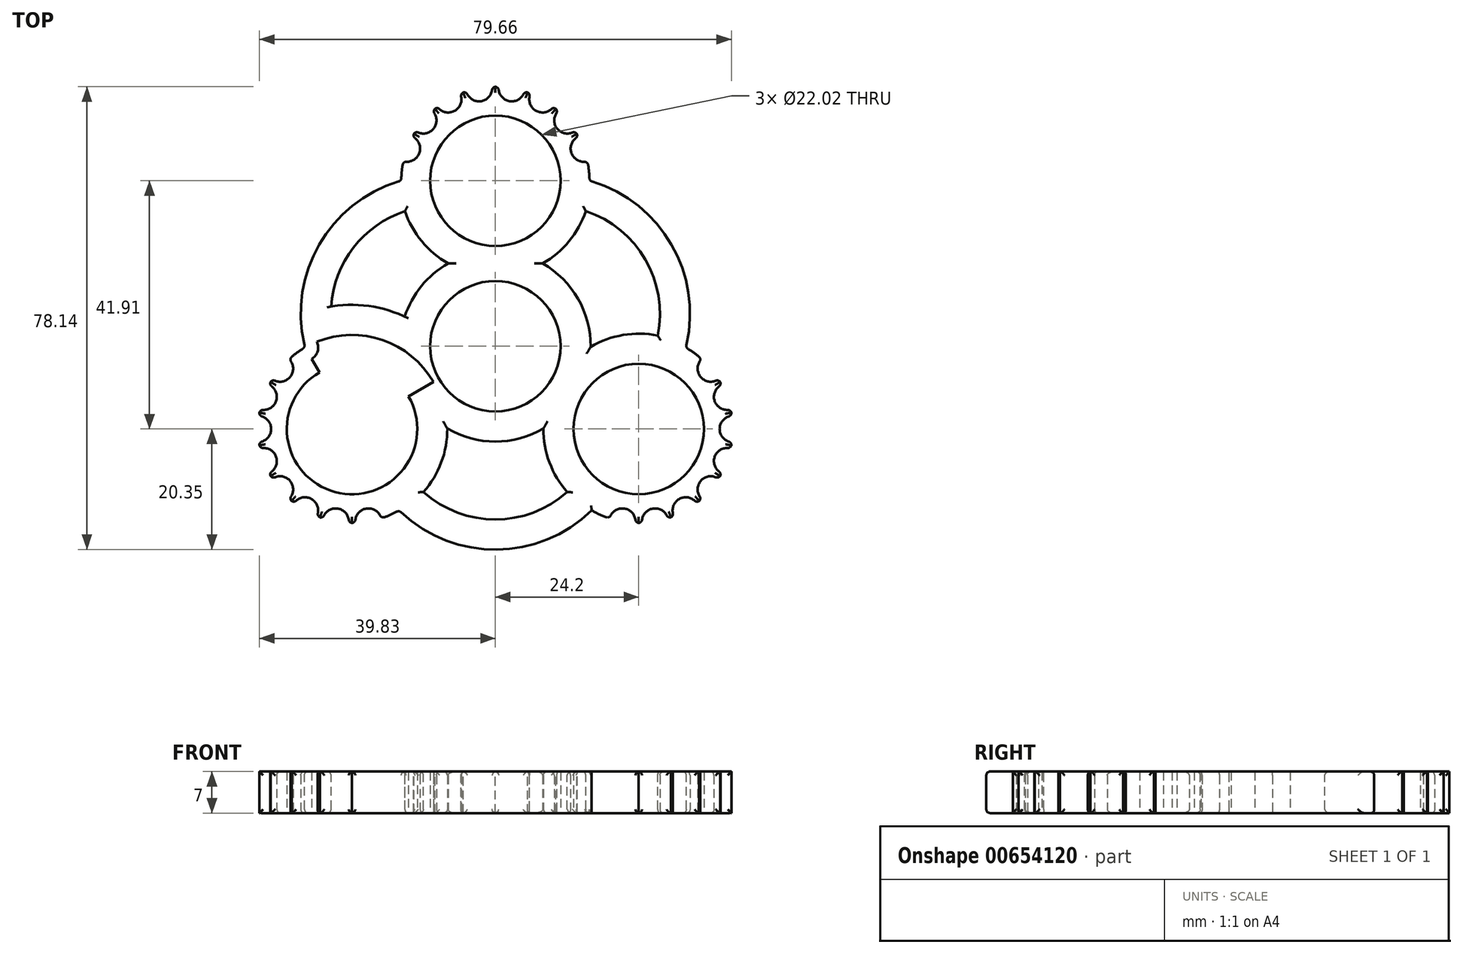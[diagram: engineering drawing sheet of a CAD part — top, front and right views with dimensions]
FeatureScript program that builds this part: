
annotation { "Feature Type Name" : "Feature", "Feature Type Description" : "" }
export const myFeature = defineFeature(function(context is Context, id is Id, definition is map)
    precondition{}
    {
        {
            var Q0;
            Q0=qCreatedBy(makeId("Top.planeOp"),FACE);
            var sketch = newSketch(context, id + "F0", { "sketchPlane" : qUnion([Q0])});
            skCircle(sketch, "E0", {"center": v(0, 0) * mm, "radius": 11.01 * mm});
            skCircle(sketch, "E1", {"center": v(0, 27.94) * mm, "radius": 11.01 * mm});
            skCircle(sketch, "E2", {"center": v(24.2, -13.97) * mm, "radius": 11.01 * mm});
            skCircle(sketch, "E3", {"center": v(-24.2, -13.97) * mm, "radius": 11.01 * mm});
            skLineSegment(sketch, "E4", {"start": v(-24.2, -13.97) * mm, "end": v(0, 0) * mm});
            skLineSegment(sketch, "E5", {"start": v(0, 0) * mm, "end": v(24.2, -13.97) * mm});
            skLineSegment(sketch, "E6", {"start": v(0, 0) * mm, "end": v(0, 27.94) * mm});
            skCircle(sketch, "E7", {"center": v(0, 27.94) * mm, "radius": 15.88 * mm});
            skCircle(sketch, "E8", {"center": v(24.2, -13.97) * mm, "radius": 15.88 * mm});
            skCircle(sketch, "E9", {"center": v(-24.2, -13.97) * mm, "radius": 15.88 * mm});
            skArc(sketch, "E10", {"start": v(-15.88, 27.94) * mm, "mid": v(-29.73, 17.16) * mm, "end": v(-32.13, -0.22) * mm});
            skArc(sketch, "E11", {"start": v(32.13, -0.22) * mm, "mid": v(29.73, 17.16) * mm, "end": v(15.88, 27.94) * mm});
            skArc(sketch, "E12", {"start": v(-16.26, -27.72) * mm, "mid": v(0, -34.32) * mm, "end": v(16.26, -27.72) * mm});
            skLineSegment(sketch, "E13", {"start": v(-15.88, 27.94) * mm, "end": v(15.88, 27.94) * mm});
            skLineSegment(sketch, "E14", {"start": v(-16.26, -27.72) * mm, "end": v(-32.13, -0.22) * mm});
            skLineSegment(sketch, "E15", {"start": v(32.13, -0.22) * mm, "end": v(16.26, -27.72) * mm});
            skLineSegment(sketch, "E16", {"start": v(-24.2, -13.97) * mm, "end": v(-37.94, -21.9) * mm});
            skLineSegment(sketch, "E17", {"start": v(0, 27.94) * mm, "end": v(0, 43.82) * mm});
            skLineSegment(sketch, "E18", {"start": v(24.2, -13.97) * mm, "end": v(37.94, -21.9) * mm});
            skCircle(sketch, "E19", {"center": v(-16.26, -27.72) * mm, "radius": 2.22 * mm});
            skCircle(sketch, "E20.1.0", {"center": v(-21.44, -29.6) * mm, "radius": 2.22 * mm});
            skCircle(sketch, "E20.2.0", {"center": v(-26.95, -29.6) * mm, "radius": 2.22 * mm});
            skCircle(sketch, "E20.3.0", {"center": v(-32.13, -27.72) * mm, "radius": 2.22 * mm});
            skCircle(sketch, "E20.4.0", {"center": v(-36.36, -24.17) * mm, "radius": 2.22 * mm});
            skCircle(sketch, "E20.5.0", {"center": v(-39.11, -19.4) * mm, "radius": 2.22 * mm});
            skCircle(sketch, "E20.6.0", {"center": v(-40.07, -13.97) * mm, "radius": 2.22 * mm});
            skCircle(sketch, "E20.7.0", {"center": v(-39.11, -8.54) * mm, "radius": 2.22 * mm});
            skCircle(sketch, "E20.8.0", {"center": v(-36.36, -3.77) * mm, "radius": 2.22 * mm});
            skCircle(sketch, "E20.9.0", {"center": v(-32.13, -0.22) * mm, "radius": 2.22 * mm});
            skLineSegment(sketch, "E20.anchor1", {"start": v(-24.2, -13.97) * mm, "end": v(-16.26, -27.72) * mm, "construction": true});
            skLineSegment(sketch, "E20.anchor2", {"start": v(-24.2, -13.97) * mm, "end": v(-32.13, -0.22) * mm, "construction": true});
            skCircle(sketch, "E21", {"center": v(-15.88, 27.94) * mm, "radius": 2.22 * mm});
            skCircle(sketch, "E22", {"center": v(32.13, -0.22) * mm, "radius": 2.22 * mm});
            skCircle(sketch, "E23.1.0", {"center": v(-14.92, 33.37) * mm, "radius": 2.22 * mm});
            skCircle(sketch, "E23.2.0", {"center": v(-12.16, 38.14) * mm, "radius": 2.22 * mm});
            skCircle(sketch, "E23.3.0", {"center": v(-7.94, 41.69) * mm, "radius": 2.22 * mm});
            skCircle(sketch, "E23.4.0", {"center": v(-2.76, 43.57) * mm, "radius": 2.22 * mm});
            skCircle(sketch, "E23.5.0", {"center": v(2.76, 43.57) * mm, "radius": 2.22 * mm});
            skCircle(sketch, "E23.6.0", {"center": v(7.94, 41.69) * mm, "radius": 2.22 * mm});
            skCircle(sketch, "E23.7.0", {"center": v(12.16, 38.14) * mm, "radius": 2.22 * mm});
            skCircle(sketch, "E23.8.0", {"center": v(14.92, 33.37) * mm, "radius": 2.22 * mm});
            skCircle(sketch, "E23.9.0", {"center": v(15.88, 27.94) * mm, "radius": 2.22 * mm});
            skLineSegment(sketch, "E23.anchor1", {"start": v(0, 27.94) * mm, "end": v(-15.88, 27.94) * mm, "construction": true});
            skLineSegment(sketch, "E23.anchor2", {"start": v(0, 27.94) * mm, "end": v(15.88, 27.94) * mm, "construction": true});
            skCircle(sketch, "E24.1.0", {"center": v(36.36, -3.77) * mm, "radius": 2.22 * mm});
            skCircle(sketch, "E24.2.0", {"center": v(39.11, -8.54) * mm, "radius": 2.22 * mm});
            skCircle(sketch, "E24.3.0", {"center": v(40.07, -13.97) * mm, "radius": 2.22 * mm});
            skCircle(sketch, "E24.4.0", {"center": v(39.11, -19.4) * mm, "radius": 2.22 * mm});
            skCircle(sketch, "E24.5.0", {"center": v(36.36, -24.17) * mm, "radius": 2.22 * mm});
            skCircle(sketch, "E24.6.0", {"center": v(32.13, -27.72) * mm, "radius": 2.22 * mm});
            skCircle(sketch, "E24.7.0", {"center": v(26.95, -29.6) * mm, "radius": 2.22 * mm});
            skCircle(sketch, "E24.8.0", {"center": v(21.44, -29.6) * mm, "radius": 2.22 * mm});
            skCircle(sketch, "E24.9.0", {"center": v(16.26, -27.72) * mm, "radius": 2.22 * mm});
            skLineSegment(sketch, "E24.anchor1", {"start": v(24.2, -13.97) * mm, "end": v(32.13, -0.22) * mm, "construction": true});
            skLineSegment(sketch, "E24.anchor2", {"start": v(24.2, -13.97) * mm, "end": v(16.26, -27.72) * mm, "construction": true});
            skSolve(sketch);
        }
        {
            var Q0;
            {var subQ1=sQuery(id+"F0.wireOp",EDGE,"E7");var subQ3=sQuery(id+"F0.wireOp",EDGE,"E23.9.0");var subQ4=makeQuery(id+"F0.imprint","INTERSECT",VERTEX,{"disambiguationData":[OD(0.0)],"derivedFrom":[subQ1,subQ3]});Q0=makeQuery(id+"F0.imprint","IMPRINT",FACE,{"disambiguationData":[TD([[makeQuery(id+"F0.imprint","IMPRINT",EDGE,{"disambiguationData":[TD([[subQ4,-1.0]])],"derivedFrom":subQ3}),1.0]])]});}
            var Q1;
            {var subQ1=sQuery(id+"F0.wireOp",EDGE,"E7");var subQ3=sQuery(id+"F0.wireOp",EDGE,"E21");var subQ4=makeQuery(id+"F0.imprint","INTERSECT",VERTEX,{"disambiguationData":[OD(0.0)],"derivedFrom":[subQ1,subQ3]});Q1=makeQuery(id+"F0.imprint","IMPRINT",FACE,{"disambiguationData":[TD([[makeQuery(id+"F0.imprint","IMPRINT",EDGE,{"disambiguationData":[TD([[subQ4,1.0]])],"derivedFrom":subQ3}),1.0]])]});}
            var Q2;
            {var subQ0=sQuery(id+"F0.wireOp",EDGE,"E10");var subQ3=sQuery(id+"F0.wireOp",EDGE,"E21");var subQ5=makeQuery(id+"F0.imprint","INTERSECT",VERTEX,{"derivedFrom":[subQ0,subQ3]});Q2=makeQuery(id+"F0.imprint","IMPRINT",FACE,{"disambiguationData":[TD([[makeQuery(id+"F0.imprint","IMPRINT",EDGE,{"disambiguationData":[TD([[subQ5,-1.0]])],"derivedFrom":subQ3}),1.0]])]});}
            var Q3;
            {var subQ0=sQuery(id+"F0.wireOp",EDGE,"E11");var subQ3=sQuery(id+"F0.wireOp",EDGE,"E23.9.0");var subQ5=makeQuery(id+"F0.imprint","INTERSECT",VERTEX,{"derivedFrom":[subQ0,subQ3]});Q3=makeQuery(id+"F0.imprint","IMPRINT",FACE,{"disambiguationData":[TD([[makeQuery(id+"F0.imprint","IMPRINT",EDGE,{"disambiguationData":[TD([[subQ5,1.0]])],"derivedFrom":subQ3}),1.0]])]});}
            var Q4;
            {var subQ1=sQuery(id+"F0.wireOp",EDGE,"E8");var subQ3=sQuery(id+"F0.wireOp",EDGE,"E22");var subQ4=makeQuery(id+"F0.imprint","INTERSECT",VERTEX,{"disambiguationData":[OD(0.0)],"derivedFrom":[subQ1,subQ3]});Q4=makeQuery(id+"F0.imprint","IMPRINT",FACE,{"disambiguationData":[TD([[makeQuery(id+"F0.imprint","IMPRINT",EDGE,{"disambiguationData":[TD([[subQ4,1.0]])],"derivedFrom":subQ3}),1.0]])]});}
            var Q5;
            {var subQ0=sQuery(id+"F0.wireOp",EDGE,"E11");var subQ3=sQuery(id+"F0.wireOp",EDGE,"E22");var subQ5=makeQuery(id+"F0.imprint","INTERSECT",VERTEX,{"derivedFrom":[subQ0,subQ3]});Q5=makeQuery(id+"F0.imprint","IMPRINT",FACE,{"disambiguationData":[TD([[makeQuery(id+"F0.imprint","IMPRINT",EDGE,{"disambiguationData":[TD([[subQ5,-1.0]])],"derivedFrom":subQ3}),1.0]])]});}
            var Q6;
            {var subQ0=sQuery(id+"F0.wireOp",EDGE,"E12");var subQ3=sQuery(id+"F0.wireOp",EDGE,"E24.9.0");var subQ5=makeQuery(id+"F0.imprint","INTERSECT",VERTEX,{"derivedFrom":[subQ0,subQ3]});Q6=makeQuery(id+"F0.imprint","IMPRINT",FACE,{"disambiguationData":[TD([[makeQuery(id+"F0.imprint","IMPRINT",EDGE,{"disambiguationData":[TD([[subQ5,1.0]])],"derivedFrom":subQ3}),1.0]])]});}
            var Q7;
            {var subQ1=sQuery(id+"F0.wireOp",EDGE,"E8");var subQ3=sQuery(id+"F0.wireOp",EDGE,"E24.9.0");var subQ4=makeQuery(id+"F0.imprint","INTERSECT",VERTEX,{"disambiguationData":[OD(0.0)],"derivedFrom":[subQ1,subQ3]});Q7=makeQuery(id+"F0.imprint","IMPRINT",FACE,{"disambiguationData":[TD([[makeQuery(id+"F0.imprint","IMPRINT",EDGE,{"disambiguationData":[TD([[subQ4,-1.0]])],"derivedFrom":subQ3}),1.0]])]});}
            var Q8;
            {var subQ0=sQuery(id+"F0.wireOp",EDGE,"E10");var subQ3=sQuery(id+"F0.wireOp",EDGE,"E20.9.0");var subQ5=makeQuery(id+"F0.imprint","INTERSECT",VERTEX,{"derivedFrom":[subQ0,subQ3]});Q8=makeQuery(id+"F0.imprint","IMPRINT",FACE,{"disambiguationData":[TD([[makeQuery(id+"F0.imprint","IMPRINT",EDGE,{"disambiguationData":[TD([[subQ5,1.0]])],"derivedFrom":subQ3}),1.0]])]});}
            var Q9;
            {var subQ1=sQuery(id+"F0.wireOp",EDGE,"E9");var subQ3=sQuery(id+"F0.wireOp",EDGE,"E20.9.0");var subQ4=makeQuery(id+"F0.imprint","INTERSECT",VERTEX,{"disambiguationData":[OD(0.0)],"derivedFrom":[subQ1,subQ3]});Q9=makeQuery(id+"F0.imprint","IMPRINT",FACE,{"disambiguationData":[TD([[makeQuery(id+"F0.imprint","IMPRINT",EDGE,{"disambiguationData":[TD([[subQ4,-1.0]])],"derivedFrom":subQ3}),1.0]])]});}
            var Q10;
            {var subQ1=sQuery(id+"F0.wireOp",EDGE,"E9");var subQ3=sQuery(id+"F0.wireOp",EDGE,"E19");var subQ4=makeQuery(id+"F0.imprint","INTERSECT",VERTEX,{"disambiguationData":[OD(0.0)],"derivedFrom":[subQ1,subQ3]});Q10=makeQuery(id+"F0.imprint","IMPRINT",FACE,{"disambiguationData":[TD([[makeQuery(id+"F0.imprint","IMPRINT",EDGE,{"disambiguationData":[TD([[subQ4,1.0]])],"derivedFrom":subQ3}),1.0]])]});}
            var Q11;
            {var subQ0=sQuery(id+"F0.wireOp",EDGE,"E12");var subQ3=sQuery(id+"F0.wireOp",EDGE,"E19");var subQ5=makeQuery(id+"F0.imprint","INTERSECT",VERTEX,{"derivedFrom":[subQ0,subQ3]});Q11=makeQuery(id+"F0.imprint","IMPRINT",FACE,{"disambiguationData":[TD([[makeQuery(id+"F0.imprint","IMPRINT",EDGE,{"disambiguationData":[TD([[subQ5,-1.0]])],"derivedFrom":subQ3}),1.0]])]});}
            var Q12;
            {var subQ7=sQuery(id+"F0.wireOp",EDGE,"E0");var subQ9=sQuery(id+"F0.wireOp",EDGE,"E4");var subQ10=makeQuery(id+"F0.imprint","INTERSECT",VERTEX,{"derivedFrom":[subQ7,subQ9]});Q12=makeQuery(id+"F0.imprint","IMPRINT",FACE,{"disambiguationData":[TD([[makeQuery(id+"F0.imprint","IMPRINT",EDGE,{"disambiguationData":[TD([[subQ10,1.0]])],"derivedFrom":subQ7}),-1.0]])]});}
            var Q13;
            {var subQ5=sQuery(id+"F0.wireOp",EDGE,"E0");var subQ7=sQuery(id+"F0.wireOp",EDGE,"E4");var subQ8=makeQuery(id+"F0.imprint","INTERSECT",VERTEX,{"derivedFrom":[subQ5,subQ7]});Q13=makeQuery(id+"F0.imprint","IMPRINT",FACE,{"disambiguationData":[TD([[makeQuery(id+"F0.imprint","IMPRINT",EDGE,{"disambiguationData":[TD([[subQ8,-1.0]])],"derivedFrom":subQ5}),-1.0]])]});}
            var Q14;
            {var subQ1=sQuery(id+"F0.wireOp",EDGE,"E6");var subQ7=sQuery(id+"F0.wireOp",EDGE,"E0");var subQ8=makeQuery(id+"F0.imprint","INTERSECT",VERTEX,{"derivedFrom":[subQ7,subQ1]});Q14=makeQuery(id+"F0.imprint","IMPRINT",FACE,{"disambiguationData":[TD([[makeQuery(id+"F0.imprint","IMPRINT",EDGE,{"disambiguationData":[TD([[subQ8,1.0]])],"derivedFrom":subQ7}),-1.0]])]});}
            var Q15;
            {var subQ1=sQuery(id+"F0.wireOp",EDGE,"E1");var subQ10=sQuery(id+"F0.wireOp",EDGE,"E17");var subQ13=makeQuery(id+"F0.imprint","INTERSECT",VERTEX,{"derivedFrom":[subQ1,subQ10]});Q15=makeQuery(id+"F0.imprint","IMPRINT",FACE,{"disambiguationData":[TD([[makeQuery(id+"F0.imprint","IMPRINT",EDGE,{"disambiguationData":[TD([[subQ13,1.0]])],"derivedFrom":subQ1}),-1.0]])]});}
            var Q16;
            {var subQ4=sQuery(id+"F0.wireOp",EDGE,"E17");var subQ5=sQuery(id+"F0.wireOp",EDGE,"E1");var subQ6=makeQuery(id+"F0.imprint","INTERSECT",VERTEX,{"derivedFrom":[subQ5,subQ4]});Q16=makeQuery(id+"F0.imprint","IMPRINT",FACE,{"disambiguationData":[TD([[makeQuery(id+"F0.imprint","IMPRINT",EDGE,{"disambiguationData":[TD([[subQ6,-1.0]])],"derivedFrom":subQ5}),-1.0]])]});}
            var Q17;
            {var subQ6=sQuery(id+"F0.wireOp",EDGE,"E2");var subQ12=sQuery(id+"F0.wireOp",EDGE,"E15");var subQ13=makeQuery(id+"F0.imprint","INTERSECT",VERTEX,{"disambiguationData":[OD(1.0)],"derivedFrom":[subQ6,subQ12]});Q17=makeQuery(id+"F0.imprint","IMPRINT",FACE,{"disambiguationData":[TD([[makeQuery(id+"F0.imprint","IMPRINT",EDGE,{"disambiguationData":[TD([[subQ13,-1.0]])],"derivedFrom":subQ6}),-1.0]])]});}
            var Q18;
            {var subQ6=sQuery(id+"F0.wireOp",EDGE,"E15");var subQ15=sQuery(id+"F0.wireOp",EDGE,"E2");var subQ17=makeQuery(id+"F0.imprint","INTERSECT",VERTEX,{"disambiguationData":[OD(0.0)],"derivedFrom":[subQ15,subQ6]});Q18=makeQuery(id+"F0.imprint","IMPRINT",FACE,{"disambiguationData":[TD([[makeQuery(id+"F0.imprint","IMPRINT",EDGE,{"disambiguationData":[TD([[subQ17,1.0]])],"derivedFrom":subQ15}),-1.0]])]});}
            var Q19;
            {var subQ3=sQuery(id+"F0.wireOp",EDGE,"E3");var subQ5=sQuery(id+"F0.wireOp",EDGE,"E14");var subQ6=makeQuery(id+"F0.imprint","INTERSECT",VERTEX,{"disambiguationData":[OD(0.0)],"derivedFrom":[subQ3,subQ5]});Q19=makeQuery(id+"F0.imprint","IMPRINT",FACE,{"disambiguationData":[TD([[makeQuery(id+"F0.imprint","IMPRINT",EDGE,{"disambiguationData":[TD([[subQ6,-1.0]])],"derivedFrom":subQ3}),-1.0]])]});}
            var Q20;
            {var subQ4=sQuery(id+"F0.wireOp",EDGE,"E16");var subQ6=sQuery(id+"F0.wireOp",EDGE,"E3");var subQ7=makeQuery(id+"F0.imprint","INTERSECT",VERTEX,{"derivedFrom":[subQ6,subQ4]});Q20=makeQuery(id+"F0.imprint","IMPRINT",FACE,{"disambiguationData":[TD([[makeQuery(id+"F0.imprint","IMPRINT",EDGE,{"disambiguationData":[TD([[subQ7,-1.0]])],"derivedFrom":subQ6}),-1.0]])]});}
            var Q21;
            {var subQ0=sQuery(id+"F0.wireOp",EDGE,"E13");var subQ1=sQuery(id+"F0.wireOp",EDGE,"E1");var subQ2=makeQuery(id+"F0.imprint","INTERSECT",VERTEX,{"disambiguationData":[OD(1.0)],"derivedFrom":[subQ1,subQ0]});Q21=makeQuery(id+"F0.imprint","IMPRINT",FACE,{"disambiguationData":[TD([[makeQuery(id+"F0.imprint","IMPRINT",EDGE,{"disambiguationData":[TD([[subQ2,-1.0]])],"derivedFrom":subQ1}),-1.0]])]});}
            var Q22;
            {var subQ1=sQuery(id+"F0.wireOp",EDGE,"E7");var subQ3=sQuery(id+"F0.wireOp",EDGE,"E21");var subQ4=makeQuery(id+"F0.imprint","INTERSECT",VERTEX,{"disambiguationData":[OD(1.0)],"derivedFrom":[subQ1,subQ3]});Q22=makeQuery(id+"F0.imprint","IMPRINT",FACE,{"disambiguationData":[TD([[makeQuery(id+"F0.imprint","IMPRINT",EDGE,{"disambiguationData":[TD([[subQ4,-1.0]])],"derivedFrom":subQ3}),1.0]])]});}
            var Q23;
            {var subQ1=sQuery(id+"F0.wireOp",EDGE,"E7");var subQ3=sQuery(id+"F0.wireOp",EDGE,"E23.9.0");var subQ4=makeQuery(id+"F0.imprint","INTERSECT",VERTEX,{"disambiguationData":[OD(1.0)],"derivedFrom":[subQ1,subQ3]});Q23=makeQuery(id+"F0.imprint","IMPRINT",FACE,{"disambiguationData":[TD([[makeQuery(id+"F0.imprint","IMPRINT",EDGE,{"disambiguationData":[TD([[subQ4,1.0]])],"derivedFrom":subQ3}),1.0]])]});}
            var Q24;
            {var subQ0=sQuery(id+"F0.wireOp",EDGE,"E13");var subQ1=sQuery(id+"F0.wireOp",EDGE,"E1");var subQ2=makeQuery(id+"F0.imprint","INTERSECT",VERTEX,{"disambiguationData":[OD(0.0)],"derivedFrom":[subQ1,subQ0]});Q24=makeQuery(id+"F0.imprint","IMPRINT",FACE,{"disambiguationData":[TD([[makeQuery(id+"F0.imprint","IMPRINT",EDGE,{"disambiguationData":[TD([[subQ2,1.0]])],"derivedFrom":subQ1}),-1.0]])]});}
            var Q25;
            {var subQ1=sQuery(id+"F0.wireOp",EDGE,"E5");var subQ6=sQuery(id+"F0.wireOp",EDGE,"E2");var subQ9=makeQuery(id+"F0.imprint","INTERSECT",VERTEX,{"derivedFrom":[subQ6,subQ1]});Q25=makeQuery(id+"F0.imprint","IMPRINT",FACE,{"disambiguationData":[TD([[makeQuery(id+"F0.imprint","IMPRINT",EDGE,{"disambiguationData":[TD([[subQ9,1.0]])],"derivedFrom":subQ6}),-1.0]])]});}
            var Q26;
            {var subQ1=sQuery(id+"F0.wireOp",EDGE,"E2");var subQ6=sQuery(id+"F0.wireOp",EDGE,"E5");var subQ9=makeQuery(id+"F0.imprint","INTERSECT",VERTEX,{"derivedFrom":[subQ1,subQ6]});Q26=makeQuery(id+"F0.imprint","IMPRINT",FACE,{"disambiguationData":[TD([[makeQuery(id+"F0.imprint","IMPRINT",EDGE,{"disambiguationData":[TD([[subQ9,-1.0]])],"derivedFrom":subQ1}),-1.0]])]});}
            var Q27;
            {var subQ1=sQuery(id+"F0.wireOp",EDGE,"E3");var subQ5=sQuery(id+"F0.wireOp",EDGE,"E4");var subQ6=makeQuery(id+"F0.imprint","INTERSECT",VERTEX,{"derivedFrom":[subQ1,subQ5]});Q27=makeQuery(id+"F0.imprint","IMPRINT",FACE,{"disambiguationData":[TD([[makeQuery(id+"F0.imprint","IMPRINT",EDGE,{"disambiguationData":[TD([[subQ6,1.0]])],"derivedFrom":subQ1}),-1.0]])]});}
            var Q28;
            {var subQ1=sQuery(id+"F0.wireOp",EDGE,"E9");var subQ3=sQuery(id+"F0.wireOp",EDGE,"E19");var subQ4=makeQuery(id+"F0.imprint","INTERSECT",VERTEX,{"disambiguationData":[OD(1.0)],"derivedFrom":[subQ1,subQ3]});Q28=makeQuery(id+"F0.imprint","IMPRINT",FACE,{"disambiguationData":[TD([[makeQuery(id+"F0.imprint","IMPRINT",EDGE,{"disambiguationData":[TD([[subQ4,-1.0]])],"derivedFrom":subQ3}),1.0]])]});}
            var Q29;
            {var subQ1=sQuery(id+"F0.wireOp",EDGE,"E9");var subQ3=sQuery(id+"F0.wireOp",EDGE,"E20.9.0");var subQ4=makeQuery(id+"F0.imprint","INTERSECT",VERTEX,{"disambiguationData":[OD(1.0)],"derivedFrom":[subQ1,subQ3]});Q29=makeQuery(id+"F0.imprint","IMPRINT",FACE,{"disambiguationData":[TD([[makeQuery(id+"F0.imprint","IMPRINT",EDGE,{"disambiguationData":[TD([[subQ4,1.0]])],"derivedFrom":subQ3}),1.0]])]});}
            var Q30;
            {var subQ0=sQuery(id+"F0.wireOp",EDGE,"E14");var subQ1=sQuery(id+"F0.wireOp",EDGE,"E3");var subQ2=makeQuery(id+"F0.imprint","INTERSECT",VERTEX,{"disambiguationData":[OD(0.0)],"derivedFrom":[subQ1,subQ0]});Q30=makeQuery(id+"F0.imprint","IMPRINT",FACE,{"disambiguationData":[TD([[makeQuery(id+"F0.imprint","IMPRINT",EDGE,{"disambiguationData":[TD([[subQ2,1.0]])],"derivedFrom":subQ1}),-1.0]])]});}
            var Q31;
            {var subQ1=sQuery(id+"F0.wireOp",EDGE,"E8");var subQ3=sQuery(id+"F0.wireOp",EDGE,"E24.9.0");var subQ4=makeQuery(id+"F0.imprint","INTERSECT",VERTEX,{"disambiguationData":[OD(1.0)],"derivedFrom":[subQ1,subQ3]});Q31=makeQuery(id+"F0.imprint","IMPRINT",FACE,{"disambiguationData":[TD([[makeQuery(id+"F0.imprint","IMPRINT",EDGE,{"disambiguationData":[TD([[subQ4,1.0]])],"derivedFrom":subQ3}),1.0]])]});}
            var Q32;
            {var subQ1=sQuery(id+"F0.wireOp",EDGE,"E8");var subQ3=sQuery(id+"F0.wireOp",EDGE,"E22");var subQ4=makeQuery(id+"F0.imprint","INTERSECT",VERTEX,{"disambiguationData":[OD(1.0)],"derivedFrom":[subQ1,subQ3]});Q32=makeQuery(id+"F0.imprint","IMPRINT",FACE,{"disambiguationData":[TD([[makeQuery(id+"F0.imprint","IMPRINT",EDGE,{"disambiguationData":[TD([[subQ4,-1.0]])],"derivedFrom":subQ3}),1.0]])]});}
            extrude(context, id + "F1", {"entities" : qUnion([Q0, Q1, Q2, Q3, Q4, Q5, Q6, Q7, Q8, Q9, Q10, Q11, Q12, Q13, Q14, Q15, Q16, Q17, Q18, Q19, Q20, Q21, Q22, Q23, Q24, Q25, Q26, Q27, Q28, Q29, Q30, Q31, Q32]), "depth" : 7 * mm, "offsetDistance" : 25.4 * mm});
        }
        {
            var Q0;
            Q0=makeQuery(id+"F1.opExtrude","CAP_FACE",FACE,{"disambiguationData":[OSD([sQuery(id+"F0.wireOp",EDGE,"E0"),sQuery(id+"F0.wireOp",EDGE,"E1"),sQuery(id+"F0.wireOp",EDGE,"E2"),sQuery(id+"F0.wireOp",EDGE,"E3"),sQuery(id+"F0.wireOp",EDGE,"E7"),sQuery(id+"F0.wireOp",EDGE,"E8"),sQuery(id+"F0.wireOp",EDGE,"E9"),sQuery(id+"F0.wireOp",EDGE,"E10"),sQuery(id+"F0.wireOp",EDGE,"E11"),sQuery(id+"F0.wireOp",EDGE,"E12"),sQuery(id+"F0.wireOp",EDGE,"E20.1.0"),sQuery(id+"F0.wireOp",EDGE,"E20.2.0"),sQuery(id+"F0.wireOp",EDGE,"E20.3.0"),sQuery(id+"F0.wireOp",EDGE,"E20.4.0"),sQuery(id+"F0.wireOp",EDGE,"E20.5.0"),sQuery(id+"F0.wireOp",EDGE,"E20.6.0"),sQuery(id+"F0.wireOp",EDGE,"E20.7.0"),sQuery(id+"F0.wireOp",EDGE,"E20.8.0"),sQuery(id+"F0.wireOp",EDGE,"E23.1.0"),sQuery(id+"F0.wireOp",EDGE,"E23.2.0"),sQuery(id+"F0.wireOp",EDGE,"E23.3.0"),sQuery(id+"F0.wireOp",EDGE,"E23.4.0"),sQuery(id+"F0.wireOp",EDGE,"E23.5.0"),sQuery(id+"F0.wireOp",EDGE,"E23.6.0"),sQuery(id+"F0.wireOp",EDGE,"E23.7.0"),sQuery(id+"F0.wireOp",EDGE,"E23.8.0"),sQuery(id+"F0.wireOp",EDGE,"E24.1.0"),sQuery(id+"F0.wireOp",EDGE,"E24.2.0"),sQuery(id+"F0.wireOp",EDGE,"E24.3.0"),sQuery(id+"F0.wireOp",EDGE,"E24.4.0"),sQuery(id+"F0.wireOp",EDGE,"E24.5.0"),sQuery(id+"F0.wireOp",EDGE,"E24.6.0"),sQuery(id+"F0.wireOp",EDGE,"E24.7.0"),sQuery(id+"F0.wireOp",EDGE,"E24.8.0")])],"isStart":false});
            var Q1;
            Q1=makeQuery(id+"F1.opExtrude","CAP_FACE",FACE,{"disambiguationData":[OSD([sQuery(id+"F0.wireOp",EDGE,"E0"),sQuery(id+"F0.wireOp",EDGE,"E1"),sQuery(id+"F0.wireOp",EDGE,"E2"),sQuery(id+"F0.wireOp",EDGE,"E3"),sQuery(id+"F0.wireOp",EDGE,"E7"),sQuery(id+"F0.wireOp",EDGE,"E8"),sQuery(id+"F0.wireOp",EDGE,"E9"),sQuery(id+"F0.wireOp",EDGE,"E10"),sQuery(id+"F0.wireOp",EDGE,"E11"),sQuery(id+"F0.wireOp",EDGE,"E12"),sQuery(id+"F0.wireOp",EDGE,"E20.1.0"),sQuery(id+"F0.wireOp",EDGE,"E20.2.0"),sQuery(id+"F0.wireOp",EDGE,"E20.3.0"),sQuery(id+"F0.wireOp",EDGE,"E20.4.0"),sQuery(id+"F0.wireOp",EDGE,"E20.5.0"),sQuery(id+"F0.wireOp",EDGE,"E20.6.0"),sQuery(id+"F0.wireOp",EDGE,"E20.7.0"),sQuery(id+"F0.wireOp",EDGE,"E20.8.0"),sQuery(id+"F0.wireOp",EDGE,"E23.1.0"),sQuery(id+"F0.wireOp",EDGE,"E23.2.0"),sQuery(id+"F0.wireOp",EDGE,"E23.3.0"),sQuery(id+"F0.wireOp",EDGE,"E23.4.0"),sQuery(id+"F0.wireOp",EDGE,"E23.5.0"),sQuery(id+"F0.wireOp",EDGE,"E23.6.0"),sQuery(id+"F0.wireOp",EDGE,"E23.7.0"),sQuery(id+"F0.wireOp",EDGE,"E23.8.0"),sQuery(id+"F0.wireOp",EDGE,"E24.1.0"),sQuery(id+"F0.wireOp",EDGE,"E24.2.0"),sQuery(id+"F0.wireOp",EDGE,"E24.3.0"),sQuery(id+"F0.wireOp",EDGE,"E24.4.0"),sQuery(id+"F0.wireOp",EDGE,"E24.5.0"),sQuery(id+"F0.wireOp",EDGE,"E24.6.0"),sQuery(id+"F0.wireOp",EDGE,"E24.7.0"),sQuery(id+"F0.wireOp",EDGE,"E24.8.0")])],"isStart":true});
            shell(context, id + "F2", {"entities" : qUnion([Q0, Q1]), "thickness" : 5.08 * mm});
        }
        {
            var Q0;
            {var subQ0=sQuery(id+"F0.wireOp",EDGE,"E23.8.0");var subQ1=sQuery(id+"F0.wireOp",EDGE,"E7");Q0=makeQuery(id+"F1.opExtrude","SWEPT_EDGE",EDGE,{"disambiguationData":[OSD([subQ1,subQ0]),TDD([makeQuery(id+"F0.imprint","INTERSECT",VERTEX,{"disambiguationData":[OD(0.0)],"derivedFrom":[subQ1,subQ0]})])]});}
            var Q1;
            {var subQ0=sQuery(id+"F0.wireOp",EDGE,"E23.8.0");var subQ1=sQuery(id+"F0.wireOp",EDGE,"E7");Q1=makeQuery(id+"F1.opExtrude","SWEPT_EDGE",EDGE,{"disambiguationData":[OSD([subQ1,subQ0]),TDD([makeQuery(id+"F0.imprint","INTERSECT",VERTEX,{"disambiguationData":[OD(1.0)],"derivedFrom":[subQ1,subQ0]})])]});}
            var Q2;
            {var subQ0=sQuery(id+"F0.wireOp",EDGE,"E23.7.0");var subQ1=sQuery(id+"F0.wireOp",EDGE,"E7");Q2=makeQuery(id+"F1.opExtrude","SWEPT_EDGE",EDGE,{"disambiguationData":[OSD([subQ1,subQ0]),TDD([makeQuery(id+"F0.imprint","INTERSECT",VERTEX,{"disambiguationData":[OD(0.0)],"derivedFrom":[subQ1,subQ0]})])]});}
            var Q3;
            {var subQ0=sQuery(id+"F0.wireOp",EDGE,"E23.7.0");var subQ1=sQuery(id+"F0.wireOp",EDGE,"E7");Q3=makeQuery(id+"F1.opExtrude","SWEPT_EDGE",EDGE,{"disambiguationData":[OSD([subQ1,subQ0]),TDD([makeQuery(id+"F0.imprint","INTERSECT",VERTEX,{"disambiguationData":[OD(1.0)],"derivedFrom":[subQ1,subQ0]})])]});}
            var Q4;
            {var subQ0=sQuery(id+"F0.wireOp",EDGE,"E23.6.0");var subQ1=sQuery(id+"F0.wireOp",EDGE,"E7");Q4=makeQuery(id+"F1.opExtrude","SWEPT_EDGE",EDGE,{"disambiguationData":[OSD([subQ1,subQ0]),TDD([makeQuery(id+"F0.imprint","INTERSECT",VERTEX,{"disambiguationData":[OD(0.0)],"derivedFrom":[subQ1,subQ0]})])]});}
            var Q5;
            {var subQ0=sQuery(id+"F0.wireOp",EDGE,"E23.6.0");var subQ1=sQuery(id+"F0.wireOp",EDGE,"E7");Q5=makeQuery(id+"F1.opExtrude","SWEPT_EDGE",EDGE,{"disambiguationData":[OSD([subQ1,subQ0]),TDD([makeQuery(id+"F0.imprint","INTERSECT",VERTEX,{"disambiguationData":[OD(1.0)],"derivedFrom":[subQ1,subQ0]})])]});}
            var Q6;
            {var subQ0=sQuery(id+"F0.wireOp",EDGE,"E23.5.0");var subQ1=sQuery(id+"F0.wireOp",EDGE,"E7");Q6=makeQuery(id+"F1.opExtrude","SWEPT_EDGE",EDGE,{"disambiguationData":[OSD([subQ1,subQ0]),TDD([makeQuery(id+"F0.imprint","INTERSECT",VERTEX,{"disambiguationData":[OD(0.0)],"derivedFrom":[subQ1,subQ0]})])]});}
            var Q7;
            {var subQ0=sQuery(id+"F0.wireOp",EDGE,"E23.5.0");var subQ1=sQuery(id+"F0.wireOp",EDGE,"E7");Q7=makeQuery(id+"F1.opExtrude","SWEPT_EDGE",EDGE,{"disambiguationData":[OSD([subQ1,subQ0]),TDD([makeQuery(id+"F0.imprint","INTERSECT",VERTEX,{"disambiguationData":[OD(1.0)],"derivedFrom":[subQ1,subQ0]})])]});}
            var Q8;
            {var subQ0=sQuery(id+"F0.wireOp",EDGE,"E23.4.0");var subQ1=sQuery(id+"F0.wireOp",EDGE,"E7");Q8=makeQuery(id+"F1.opExtrude","SWEPT_EDGE",EDGE,{"disambiguationData":[OSD([subQ1,subQ0]),TDD([makeQuery(id+"F0.imprint","INTERSECT",VERTEX,{"disambiguationData":[OD(0.0)],"derivedFrom":[subQ1,subQ0]})])]});}
            var Q9;
            {var subQ0=sQuery(id+"F0.wireOp",EDGE,"E23.4.0");var subQ1=sQuery(id+"F0.wireOp",EDGE,"E7");Q9=makeQuery(id+"F1.opExtrude","SWEPT_EDGE",EDGE,{"disambiguationData":[OSD([subQ1,subQ0]),TDD([makeQuery(id+"F0.imprint","INTERSECT",VERTEX,{"disambiguationData":[OD(1.0)],"derivedFrom":[subQ1,subQ0]})])]});}
            var Q10;
            {var subQ0=sQuery(id+"F0.wireOp",EDGE,"E24.1.0");var subQ1=sQuery(id+"F0.wireOp",EDGE,"E8");Q10=makeQuery(id+"F1.opExtrude","SWEPT_EDGE",EDGE,{"disambiguationData":[OSD([subQ1,subQ0]),TDD([makeQuery(id+"F0.imprint","INTERSECT",VERTEX,{"disambiguationData":[OD(1.0)],"derivedFrom":[subQ1,subQ0]})])]});}
            var Q11;
            {var subQ0=sQuery(id+"F0.wireOp",EDGE,"E24.1.0");var subQ1=sQuery(id+"F0.wireOp",EDGE,"E8");Q11=makeQuery(id+"F1.opExtrude","SWEPT_EDGE",EDGE,{"disambiguationData":[OSD([subQ1,subQ0]),TDD([makeQuery(id+"F0.imprint","INTERSECT",VERTEX,{"disambiguationData":[OD(0.0)],"derivedFrom":[subQ1,subQ0]})])]});}
            var Q12;
            {var subQ0=sQuery(id+"F0.wireOp",EDGE,"E24.2.0");var subQ1=sQuery(id+"F0.wireOp",EDGE,"E8");Q12=makeQuery(id+"F1.opExtrude","SWEPT_EDGE",EDGE,{"disambiguationData":[OSD([subQ1,subQ0]),TDD([makeQuery(id+"F0.imprint","INTERSECT",VERTEX,{"disambiguationData":[OD(0.0)],"derivedFrom":[subQ1,subQ0]})])]});}
            var Q13;
            {var subQ0=sQuery(id+"F0.wireOp",EDGE,"E24.2.0");var subQ1=sQuery(id+"F0.wireOp",EDGE,"E8");Q13=makeQuery(id+"F1.opExtrude","SWEPT_EDGE",EDGE,{"disambiguationData":[OSD([subQ1,subQ0]),TDD([makeQuery(id+"F0.imprint","INTERSECT",VERTEX,{"disambiguationData":[OD(1.0)],"derivedFrom":[subQ1,subQ0]})])]});}
            var Q14;
            {var subQ0=sQuery(id+"F0.wireOp",EDGE,"E24.3.0");var subQ1=sQuery(id+"F0.wireOp",EDGE,"E8");Q14=makeQuery(id+"F1.opExtrude","SWEPT_EDGE",EDGE,{"disambiguationData":[OSD([subQ1,subQ0]),TDD([makeQuery(id+"F0.imprint","INTERSECT",VERTEX,{"disambiguationData":[OD(0.0)],"derivedFrom":[subQ1,subQ0]})])]});}
            var Q15;
            {var subQ0=sQuery(id+"F0.wireOp",EDGE,"E24.4.0");var subQ1=sQuery(id+"F0.wireOp",EDGE,"E8");Q15=makeQuery(id+"F1.opExtrude","SWEPT_EDGE",EDGE,{"disambiguationData":[OSD([subQ1,subQ0]),TDD([makeQuery(id+"F0.imprint","INTERSECT",VERTEX,{"disambiguationData":[OD(0.0)],"derivedFrom":[subQ1,subQ0]})])]});}
            var Q16;
            {var subQ0=sQuery(id+"F0.wireOp",EDGE,"E24.5.0");var subQ1=sQuery(id+"F0.wireOp",EDGE,"E8");Q16=makeQuery(id+"F1.opExtrude","SWEPT_EDGE",EDGE,{"disambiguationData":[OSD([subQ1,subQ0]),TDD([makeQuery(id+"F0.imprint","INTERSECT",VERTEX,{"disambiguationData":[OD(1.0)],"derivedFrom":[subQ1,subQ0]})])]});}
            var Q17;
            {var subQ0=sQuery(id+"F0.wireOp",EDGE,"E24.3.0");var subQ1=sQuery(id+"F0.wireOp",EDGE,"E8");Q17=makeQuery(id+"F1.opExtrude","SWEPT_EDGE",EDGE,{"disambiguationData":[OSD([subQ1,subQ0]),TDD([makeQuery(id+"F0.imprint","INTERSECT",VERTEX,{"disambiguationData":[OD(1.0)],"derivedFrom":[subQ1,subQ0]})])]});}
            var Q18;
            {var subQ0=sQuery(id+"F0.wireOp",EDGE,"E24.4.0");var subQ1=sQuery(id+"F0.wireOp",EDGE,"E8");Q18=makeQuery(id+"F1.opExtrude","SWEPT_EDGE",EDGE,{"disambiguationData":[OSD([subQ1,subQ0]),TDD([makeQuery(id+"F0.imprint","INTERSECT",VERTEX,{"disambiguationData":[OD(1.0)],"derivedFrom":[subQ1,subQ0]})])]});}
            var Q19;
            Q19=makeQuery(id+"F1.opExtrude","SWEPT_EDGE",EDGE,{"disambiguationData":[OSD([sQuery(id+"F0.wireOp",EDGE,"E8"),sQuery(id+"F0.wireOp",EDGE,"E11"),sQuery(id+"F0.wireOp",EDGE,"E15")])]});
            var Q20;
            Q20=makeQuery(id+"F1.opExtrude","SWEPT_EDGE",EDGE,{"disambiguationData":[OSD([sQuery(id+"F0.wireOp",EDGE,"E7"),sQuery(id+"F0.wireOp",EDGE,"E11"),sQuery(id+"F0.wireOp",EDGE,"E13")])]});
            var Q21;
            {var subQ0=sQuery(id+"F0.wireOp",EDGE,"E23.3.0");var subQ1=sQuery(id+"F0.wireOp",EDGE,"E7");Q21=makeQuery(id+"F1.opExtrude","SWEPT_EDGE",EDGE,{"disambiguationData":[OSD([subQ1,subQ0]),TDD([makeQuery(id+"F0.imprint","INTERSECT",VERTEX,{"disambiguationData":[OD(1.0)],"derivedFrom":[subQ1,subQ0]})])]});}
            var Q22;
            {var subQ0=sQuery(id+"F0.wireOp",EDGE,"E23.3.0");var subQ1=sQuery(id+"F0.wireOp",EDGE,"E7");Q22=makeQuery(id+"F1.opExtrude","SWEPT_EDGE",EDGE,{"disambiguationData":[OSD([subQ1,subQ0]),TDD([makeQuery(id+"F0.imprint","INTERSECT",VERTEX,{"disambiguationData":[OD(0.0)],"derivedFrom":[subQ1,subQ0]})])]});}
            var Q23;
            {var subQ0=sQuery(id+"F0.wireOp",EDGE,"E23.2.0");var subQ1=sQuery(id+"F0.wireOp",EDGE,"E7");Q23=makeQuery(id+"F1.opExtrude","SWEPT_EDGE",EDGE,{"disambiguationData":[OSD([subQ1,subQ0]),TDD([makeQuery(id+"F0.imprint","INTERSECT",VERTEX,{"disambiguationData":[OD(0.0)],"derivedFrom":[subQ1,subQ0]})])]});}
            var Q24;
            {var subQ0=sQuery(id+"F0.wireOp",EDGE,"E23.2.0");var subQ1=sQuery(id+"F0.wireOp",EDGE,"E7");Q24=makeQuery(id+"F1.opExtrude","SWEPT_EDGE",EDGE,{"disambiguationData":[OSD([subQ1,subQ0]),TDD([makeQuery(id+"F0.imprint","INTERSECT",VERTEX,{"disambiguationData":[OD(1.0)],"derivedFrom":[subQ1,subQ0]})])]});}
            var Q25;
            {var subQ0=sQuery(id+"F0.wireOp",EDGE,"E23.1.0");var subQ1=sQuery(id+"F0.wireOp",EDGE,"E7");Q25=makeQuery(id+"F1.opExtrude","SWEPT_EDGE",EDGE,{"disambiguationData":[OSD([subQ1,subQ0]),TDD([makeQuery(id+"F0.imprint","INTERSECT",VERTEX,{"disambiguationData":[OD(0.0)],"derivedFrom":[subQ1,subQ0]})])]});}
            var Q26;
            {var subQ0=sQuery(id+"F0.wireOp",EDGE,"E23.1.0");var subQ1=sQuery(id+"F0.wireOp",EDGE,"E7");Q26=makeQuery(id+"F1.opExtrude","SWEPT_EDGE",EDGE,{"disambiguationData":[OSD([subQ1,subQ0]),TDD([makeQuery(id+"F0.imprint","INTERSECT",VERTEX,{"disambiguationData":[OD(1.0)],"derivedFrom":[subQ1,subQ0]})])]});}
            var Q27;
            Q27=makeQuery(id+"F1.opExtrude","SWEPT_EDGE",EDGE,{"disambiguationData":[OSD([sQuery(id+"F0.wireOp",EDGE,"E7"),sQuery(id+"F0.wireOp",EDGE,"E10"),sQuery(id+"F0.wireOp",EDGE,"E13")])]});
            var Q28;
            Q28=makeQuery(id+"F1.opExtrude","SWEPT_EDGE",EDGE,{"disambiguationData":[OSD([sQuery(id+"F0.wireOp",EDGE,"E9"),sQuery(id+"F0.wireOp",EDGE,"E10"),sQuery(id+"F0.wireOp",EDGE,"E14")])]});
            var Q29;
            Q29=makeQuery(id+"F1.opExtrude","SWEPT_EDGE",EDGE,{"disambiguationData":[OSD([sQuery(id+"F0.wireOp",EDGE,"E9"),sQuery(id+"F0.wireOp",EDGE,"E12"),sQuery(id+"F0.wireOp",EDGE,"E14")])]});
            var Q30;
            {var subQ0=sQuery(id+"F0.wireOp",EDGE,"E24.6.0");var subQ1=sQuery(id+"F0.wireOp",EDGE,"E8");Q30=makeQuery(id+"F1.opExtrude","SWEPT_EDGE",EDGE,{"disambiguationData":[OSD([subQ1,subQ0]),TDD([makeQuery(id+"F0.imprint","INTERSECT",VERTEX,{"disambiguationData":[OD(0.0)],"derivedFrom":[subQ1,subQ0]})])]});}
            var Q31;
            {var subQ0=sQuery(id+"F0.wireOp",EDGE,"E24.7.0");var subQ1=sQuery(id+"F0.wireOp",EDGE,"E8");Q31=makeQuery(id+"F1.opExtrude","SWEPT_EDGE",EDGE,{"disambiguationData":[OSD([subQ1,subQ0]),TDD([makeQuery(id+"F0.imprint","INTERSECT",VERTEX,{"disambiguationData":[OD(1.0)],"derivedFrom":[subQ1,subQ0]})])]});}
            var Q32;
            {var subQ0=sQuery(id+"F0.wireOp",EDGE,"E24.7.0");var subQ1=sQuery(id+"F0.wireOp",EDGE,"E8");Q32=makeQuery(id+"F1.opExtrude","SWEPT_EDGE",EDGE,{"disambiguationData":[OSD([subQ1,subQ0]),TDD([makeQuery(id+"F0.imprint","INTERSECT",VERTEX,{"disambiguationData":[OD(0.0)],"derivedFrom":[subQ1,subQ0]})])]});}
            var Q33;
            {var subQ0=sQuery(id+"F0.wireOp",EDGE,"E24.8.0");var subQ1=sQuery(id+"F0.wireOp",EDGE,"E8");Q33=makeQuery(id+"F1.opExtrude","SWEPT_EDGE",EDGE,{"disambiguationData":[OSD([subQ1,subQ0]),TDD([makeQuery(id+"F0.imprint","INTERSECT",VERTEX,{"disambiguationData":[OD(0.0)],"derivedFrom":[subQ1,subQ0]})])]});}
            var Q34;
            {var subQ0=sQuery(id+"F0.wireOp",EDGE,"E24.8.0");var subQ1=sQuery(id+"F0.wireOp",EDGE,"E8");Q34=makeQuery(id+"F1.opExtrude","SWEPT_EDGE",EDGE,{"disambiguationData":[OSD([subQ1,subQ0]),TDD([makeQuery(id+"F0.imprint","INTERSECT",VERTEX,{"disambiguationData":[OD(1.0)],"derivedFrom":[subQ1,subQ0]})])]});}
            var Q35;
            {var subQ0=sQuery(id+"F0.wireOp",EDGE,"E24.6.0");var subQ1=sQuery(id+"F0.wireOp",EDGE,"E8");Q35=makeQuery(id+"F1.opExtrude","SWEPT_EDGE",EDGE,{"disambiguationData":[OSD([subQ1,subQ0]),TDD([makeQuery(id+"F0.imprint","INTERSECT",VERTEX,{"disambiguationData":[OD(1.0)],"derivedFrom":[subQ1,subQ0]})])]});}
            var Q36;
            {var subQ0=sQuery(id+"F0.wireOp",EDGE,"E24.5.0");var subQ1=sQuery(id+"F0.wireOp",EDGE,"E8");Q36=makeQuery(id+"F1.opExtrude","SWEPT_EDGE",EDGE,{"disambiguationData":[OSD([subQ1,subQ0]),TDD([makeQuery(id+"F0.imprint","INTERSECT",VERTEX,{"disambiguationData":[OD(0.0)],"derivedFrom":[subQ1,subQ0]})])]});}
            var Q37;
            {var subQ0=sQuery(id+"F0.wireOp",EDGE,"E20.1.0");var subQ1=sQuery(id+"F0.wireOp",EDGE,"E9");Q37=makeQuery(id+"F1.opExtrude","SWEPT_EDGE",EDGE,{"disambiguationData":[OSD([subQ1,subQ0]),TDD([makeQuery(id+"F0.imprint","INTERSECT",VERTEX,{"disambiguationData":[OD(1.0)],"derivedFrom":[subQ1,subQ0]})])]});}
            var Q38;
            {var subQ0=sQuery(id+"F0.wireOp",EDGE,"E20.2.0");var subQ1=sQuery(id+"F0.wireOp",EDGE,"E9");Q38=makeQuery(id+"F1.opExtrude","SWEPT_EDGE",EDGE,{"disambiguationData":[OSD([subQ1,subQ0]),TDD([makeQuery(id+"F0.imprint","INTERSECT",VERTEX,{"disambiguationData":[OD(0.0)],"derivedFrom":[subQ1,subQ0]})])]});}
            var Q39;
            {var subQ0=sQuery(id+"F0.wireOp",EDGE,"E20.2.0");var subQ1=sQuery(id+"F0.wireOp",EDGE,"E9");Q39=makeQuery(id+"F1.opExtrude","SWEPT_EDGE",EDGE,{"disambiguationData":[OSD([subQ1,subQ0]),TDD([makeQuery(id+"F0.imprint","INTERSECT",VERTEX,{"disambiguationData":[OD(1.0)],"derivedFrom":[subQ1,subQ0]})])]});}
            var Q40;
            Q40=makeQuery(id+"F1.opExtrude","CAP_EDGE",EDGE,{"disambiguationData":[OSD([sQuery(id+"F0.wireOp",EDGE,"E12")])],"isStart":true});
            var Q41;
            Q41=makeQuery(id+"F1.opExtrude","CAP_EDGE",EDGE,{"disambiguationData":[OSD([sQuery(id+"F0.wireOp",EDGE,"E12")])],"isStart":false});
            var Q42;
            Q42=makeQuery(id+"F1.opExtrude","CAP_EDGE",EDGE,{"disambiguationData":[OSD([sQuery(id+"F0.wireOp",EDGE,"E10")])],"isStart":true});
            var Q43;
            {var subQ0=sQuery(id+"F0.wireOp",EDGE,"E20.3.0");var subQ1=sQuery(id+"F0.wireOp",EDGE,"E9");Q43=makeQuery(id+"F1.opExtrude","SWEPT_EDGE",EDGE,{"disambiguationData":[OSD([subQ1,subQ0]),TDD([makeQuery(id+"F0.imprint","INTERSECT",VERTEX,{"disambiguationData":[OD(1.0)],"derivedFrom":[subQ1,subQ0]})])]});}
            var Q44;
            Q44=makeQuery(id+"F1.opExtrude","CAP_EDGE",EDGE,{"disambiguationData":[OSD([sQuery(id+"F0.wireOp",EDGE,"E11")])],"isStart":true});
            var Q45;
            {var subQ0=sQuery(id+"F0.wireOp",EDGE,"E20.1.0");var subQ1=sQuery(id+"F0.wireOp",EDGE,"E9");Q45=makeQuery(id+"F1.opExtrude","SWEPT_EDGE",EDGE,{"disambiguationData":[OSD([subQ1,subQ0]),TDD([makeQuery(id+"F0.imprint","INTERSECT",VERTEX,{"disambiguationData":[OD(0.0)],"derivedFrom":[subQ1,subQ0]})])]});}
            var Q46;
            {var subQ0=sQuery(id+"F0.wireOp",EDGE,"E20.7.0");var subQ1=sQuery(id+"F0.wireOp",EDGE,"E9");Q46=makeQuery(id+"F1.opExtrude","SWEPT_EDGE",EDGE,{"disambiguationData":[OSD([subQ1,subQ0]),TDD([makeQuery(id+"F0.imprint","INTERSECT",VERTEX,{"disambiguationData":[OD(1.0)],"derivedFrom":[subQ1,subQ0]})])]});}
            var Q47;
            {var subQ0=sQuery(id+"F0.wireOp",EDGE,"E20.3.0");var subQ1=sQuery(id+"F0.wireOp",EDGE,"E9");Q47=makeQuery(id+"F1.opExtrude","SWEPT_EDGE",EDGE,{"disambiguationData":[OSD([subQ1,subQ0]),TDD([makeQuery(id+"F0.imprint","INTERSECT",VERTEX,{"disambiguationData":[OD(0.0)],"derivedFrom":[subQ1,subQ0]})])]});}
            var Q48;
            {var subQ0=sQuery(id+"F0.wireOp",EDGE,"E20.5.0");var subQ1=sQuery(id+"F0.wireOp",EDGE,"E9");Q48=makeQuery(id+"F1.opExtrude","SWEPT_EDGE",EDGE,{"disambiguationData":[OSD([subQ1,subQ0]),TDD([makeQuery(id+"F0.imprint","INTERSECT",VERTEX,{"disambiguationData":[OD(1.0)],"derivedFrom":[subQ1,subQ0]})])]});}
            var Q49;
            {var subQ0=sQuery(id+"F0.wireOp",EDGE,"E20.4.0");var subQ1=sQuery(id+"F0.wireOp",EDGE,"E9");Q49=makeQuery(id+"F1.opExtrude","SWEPT_EDGE",EDGE,{"disambiguationData":[OSD([subQ1,subQ0]),TDD([makeQuery(id+"F0.imprint","INTERSECT",VERTEX,{"disambiguationData":[OD(0.0)],"derivedFrom":[subQ1,subQ0]})])]});}
            var Q50;
            {var subQ0=sQuery(id+"F0.wireOp",EDGE,"E20.6.0");var subQ1=sQuery(id+"F0.wireOp",EDGE,"E9");Q50=makeQuery(id+"F1.opExtrude","SWEPT_EDGE",EDGE,{"disambiguationData":[OSD([subQ1,subQ0]),TDD([makeQuery(id+"F0.imprint","INTERSECT",VERTEX,{"disambiguationData":[OD(1.0)],"derivedFrom":[subQ1,subQ0]})])]});}
            var Q51;
            {var subQ0=sQuery(id+"F0.wireOp",EDGE,"E20.6.0");var subQ1=sQuery(id+"F0.wireOp",EDGE,"E9");Q51=makeQuery(id+"F1.opExtrude","SWEPT_EDGE",EDGE,{"disambiguationData":[OSD([subQ1,subQ0]),TDD([makeQuery(id+"F0.imprint","INTERSECT",VERTEX,{"disambiguationData":[OD(0.0)],"derivedFrom":[subQ1,subQ0]})])]});}
            var Q52;
            {var subQ0=sQuery(id+"F0.wireOp",EDGE,"E20.5.0");var subQ1=sQuery(id+"F0.wireOp",EDGE,"E9");Q52=makeQuery(id+"F1.opExtrude","SWEPT_EDGE",EDGE,{"disambiguationData":[OSD([subQ1,subQ0]),TDD([makeQuery(id+"F0.imprint","INTERSECT",VERTEX,{"disambiguationData":[OD(0.0)],"derivedFrom":[subQ1,subQ0]})])]});}
            var Q53;
            {var subQ0=sQuery(id+"F0.wireOp",EDGE,"E20.8.0");var subQ1=sQuery(id+"F0.wireOp",EDGE,"E9");Q53=makeQuery(id+"F1.opExtrude","SWEPT_EDGE",EDGE,{"disambiguationData":[OSD([subQ1,subQ0]),TDD([makeQuery(id+"F0.imprint","INTERSECT",VERTEX,{"disambiguationData":[OD(0.0)],"derivedFrom":[subQ1,subQ0]})])]});}
            var Q54;
            {var subQ0=sQuery(id+"F0.wireOp",EDGE,"E20.8.0");var subQ1=sQuery(id+"F0.wireOp",EDGE,"E9");Q54=makeQuery(id+"F1.opExtrude","SWEPT_EDGE",EDGE,{"disambiguationData":[OSD([subQ1,subQ0]),TDD([makeQuery(id+"F0.imprint","INTERSECT",VERTEX,{"disambiguationData":[OD(1.0)],"derivedFrom":[subQ1,subQ0]})])]});}
            var Q55;
            {var subQ0=sQuery(id+"F0.wireOp",EDGE,"E20.7.0");var subQ1=sQuery(id+"F0.wireOp",EDGE,"E9");Q55=makeQuery(id+"F1.opExtrude","SWEPT_EDGE",EDGE,{"disambiguationData":[OSD([subQ1,subQ0]),TDD([makeQuery(id+"F0.imprint","INTERSECT",VERTEX,{"disambiguationData":[OD(0.0)],"derivedFrom":[subQ1,subQ0]})])]});}
            var Q56;
            Q56=makeQuery(id+"F1.opExtrude","CAP_EDGE",EDGE,{"disambiguationData":[OSD([sQuery(id+"F0.wireOp",EDGE,"E10")])],"isStart":false});
            var Q57;
            Q57=makeQuery(id+"F1.opExtrude","CAP_EDGE",EDGE,{"disambiguationData":[OSD([sQuery(id+"F0.wireOp",EDGE,"E20.5.0")])],"isStart":true});
            var Q58;
            Q58=makeQuery(id+"F1.opExtrude","CAP_EDGE",EDGE,{"disambiguationData":[OSD([sQuery(id+"F0.wireOp",EDGE,"E20.4.0")])],"isStart":true});
            var Q59;
            Q59=makeQuery(id+"F1.opExtrude","CAP_EDGE",EDGE,{"disambiguationData":[OSD([sQuery(id+"F0.wireOp",EDGE,"E20.3.0")])],"isStart":true});
            var Q60;
            Q60=makeQuery(id+"F1.opExtrude","CAP_EDGE",EDGE,{"disambiguationData":[OSD([sQuery(id+"F0.wireOp",EDGE,"E20.2.0")])],"isStart":true});
            var Q61;
            Q61=makeQuery(id+"F1.opExtrude","CAP_EDGE",EDGE,{"disambiguationData":[OSD([sQuery(id+"F0.wireOp",EDGE,"E20.1.0")])],"isStart":true});
            var Q62;
            Q62=makeQuery(id+"F1.opExtrude","CAP_EDGE",EDGE,{"disambiguationData":[OSD([sQuery(id+"F0.wireOp",EDGE,"E20.6.0")])],"isStart":true});
            var Q63;
            Q63=makeQuery(id+"F1.opExtrude","CAP_EDGE",EDGE,{"disambiguationData":[OSD([sQuery(id+"F0.wireOp",EDGE,"E20.7.0")])],"isStart":true});
            var Q64;
            Q64=makeQuery(id+"F1.opExtrude","CAP_EDGE",EDGE,{"disambiguationData":[OSD([sQuery(id+"F0.wireOp",EDGE,"E20.8.0")])],"isStart":true});
            var Q65;
            Q65=makeQuery(id+"F1.opExtrude","CAP_EDGE",EDGE,{"disambiguationData":[OSD([sQuery(id+"F0.wireOp",EDGE,"E24.8.0")])],"isStart":true});
            var Q66;
            Q66=makeQuery(id+"F1.opExtrude","CAP_EDGE",EDGE,{"disambiguationData":[OSD([sQuery(id+"F0.wireOp",EDGE,"E24.7.0")])],"isStart":true});
            var Q67;
            Q67=makeQuery(id+"F1.opExtrude","CAP_EDGE",EDGE,{"disambiguationData":[OSD([sQuery(id+"F0.wireOp",EDGE,"E24.6.0")])],"isStart":true});
            var Q68;
            Q68=makeQuery(id+"F1.opExtrude","CAP_EDGE",EDGE,{"disambiguationData":[OSD([sQuery(id+"F0.wireOp",EDGE,"E24.5.0")])],"isStart":true});
            var Q69;
            Q69=makeQuery(id+"F1.opExtrude","CAP_EDGE",EDGE,{"disambiguationData":[OSD([sQuery(id+"F0.wireOp",EDGE,"E24.4.0")])],"isStart":true});
            var Q70;
            Q70=makeQuery(id+"F1.opExtrude","CAP_EDGE",EDGE,{"disambiguationData":[OSD([sQuery(id+"F0.wireOp",EDGE,"E24.3.0")])],"isStart":true});
            var Q71;
            Q71=makeQuery(id+"F1.opExtrude","CAP_EDGE",EDGE,{"disambiguationData":[OSD([sQuery(id+"F0.wireOp",EDGE,"E24.2.0")])],"isStart":true});
            var Q72;
            Q72=makeQuery(id+"F1.opExtrude","CAP_EDGE",EDGE,{"disambiguationData":[OSD([sQuery(id+"F0.wireOp",EDGE,"E24.1.0")])],"isStart":true});
            var Q73;
            Q73=makeQuery(id+"F1.opExtrude","CAP_EDGE",EDGE,{"disambiguationData":[OSD([sQuery(id+"F0.wireOp",EDGE,"E23.8.0")])],"isStart":true});
            var Q74;
            Q74=makeQuery(id+"F1.opExtrude","CAP_EDGE",EDGE,{"disambiguationData":[OSD([sQuery(id+"F0.wireOp",EDGE,"E23.7.0")])],"isStart":true});
            var Q75;
            Q75=makeQuery(id+"F1.opExtrude","CAP_EDGE",EDGE,{"disambiguationData":[OSD([sQuery(id+"F0.wireOp",EDGE,"E23.6.0")])],"isStart":true});
            var Q76;
            Q76=makeQuery(id+"F1.opExtrude","CAP_EDGE",EDGE,{"disambiguationData":[OSD([sQuery(id+"F0.wireOp",EDGE,"E23.5.0")])],"isStart":true});
            var Q77;
            Q77=makeQuery(id+"F1.opExtrude","CAP_EDGE",EDGE,{"disambiguationData":[OSD([sQuery(id+"F0.wireOp",EDGE,"E23.4.0")])],"isStart":true});
            var Q78;
            Q78=makeQuery(id+"F1.opExtrude","CAP_EDGE",EDGE,{"disambiguationData":[OSD([sQuery(id+"F0.wireOp",EDGE,"E23.3.0")])],"isStart":true});
            var Q79;
            Q79=makeQuery(id+"F1.opExtrude","CAP_EDGE",EDGE,{"disambiguationData":[OSD([sQuery(id+"F0.wireOp",EDGE,"E23.2.0")])],"isStart":true});
            var Q80;
            Q80=makeQuery(id+"F1.opExtrude","CAP_EDGE",EDGE,{"disambiguationData":[OSD([sQuery(id+"F0.wireOp",EDGE,"E23.1.0")])],"isStart":true});
            var Q81;
            Q81=makeQuery(id+"F1.opExtrude","CAP_EDGE",EDGE,{"disambiguationData":[OSD([sQuery(id+"F0.wireOp",EDGE,"E23.1.0")])],"isStart":false});
            var Q82;
            Q82=makeQuery(id+"F1.opExtrude","CAP_EDGE",EDGE,{"disambiguationData":[OSD([sQuery(id+"F0.wireOp",EDGE,"E23.6.0")])],"isStart":false});
            var Q83;
            Q83=makeQuery(id+"F1.opExtrude","CAP_EDGE",EDGE,{"disambiguationData":[OSD([sQuery(id+"F0.wireOp",EDGE,"E23.7.0")])],"isStart":false});
            var Q84;
            Q84=makeQuery(id+"F1.opExtrude","CAP_EDGE",EDGE,{"disambiguationData":[OSD([sQuery(id+"F0.wireOp",EDGE,"E23.8.0")])],"isStart":false});
            var Q85;
            Q85=makeQuery(id+"F1.opExtrude","CAP_EDGE",EDGE,{"disambiguationData":[OSD([sQuery(id+"F0.wireOp",EDGE,"E23.2.0")])],"isStart":false});
            var Q86;
            Q86=makeQuery(id+"F1.opExtrude","CAP_EDGE",EDGE,{"disambiguationData":[OSD([sQuery(id+"F0.wireOp",EDGE,"E20.8.0")])],"isStart":false});
            var Q87;
            Q87=makeQuery(id+"F1.opExtrude","CAP_EDGE",EDGE,{"disambiguationData":[OSD([sQuery(id+"F0.wireOp",EDGE,"E23.5.0")])],"isStart":false});
            var Q88;
            Q88=makeQuery(id+"F1.opExtrude","CAP_EDGE",EDGE,{"disambiguationData":[OSD([sQuery(id+"F0.wireOp",EDGE,"E23.4.0")])],"isStart":false});
            var Q89;
            Q89=makeQuery(id+"F1.opExtrude","CAP_EDGE",EDGE,{"disambiguationData":[OSD([sQuery(id+"F0.wireOp",EDGE,"E23.3.0")])],"isStart":false});
            var Q90;
            Q90=makeQuery(id+"F1.opExtrude","CAP_EDGE",EDGE,{"disambiguationData":[OSD([sQuery(id+"F0.wireOp",EDGE,"E24.8.0")])],"isStart":false});
            var Q91;
            Q91=makeQuery(id+"F1.opExtrude","CAP_EDGE",EDGE,{"disambiguationData":[OSD([sQuery(id+"F0.wireOp",EDGE,"E24.7.0")])],"isStart":false});
            var Q92;
            Q92=makeQuery(id+"F1.opExtrude","CAP_EDGE",EDGE,{"disambiguationData":[OSD([sQuery(id+"F0.wireOp",EDGE,"E24.6.0")])],"isStart":false});
            var Q93;
            Q93=makeQuery(id+"F1.opExtrude","CAP_EDGE",EDGE,{"disambiguationData":[OSD([sQuery(id+"F0.wireOp",EDGE,"E24.5.0")])],"isStart":false});
            var Q94;
            Q94=makeQuery(id+"F1.opExtrude","CAP_EDGE",EDGE,{"disambiguationData":[OSD([sQuery(id+"F0.wireOp",EDGE,"E24.4.0")])],"isStart":false});
            var Q95;
            Q95=makeQuery(id+"F1.opExtrude","CAP_EDGE",EDGE,{"disambiguationData":[OSD([sQuery(id+"F0.wireOp",EDGE,"E24.3.0")])],"isStart":false});
            var Q96;
            Q96=makeQuery(id+"F1.opExtrude","CAP_EDGE",EDGE,{"disambiguationData":[OSD([sQuery(id+"F0.wireOp",EDGE,"E24.2.0")])],"isStart":false});
            var Q97;
            Q97=makeQuery(id+"F1.opExtrude","CAP_EDGE",EDGE,{"disambiguationData":[OSD([sQuery(id+"F0.wireOp",EDGE,"E24.1.0")])],"isStart":false});
            var Q98;
            {var subQ0=sQuery(id+"F0.wireOp",EDGE,"E9");var subQ1=makeQuery(id+"F0.imprint","INTERSECT",VERTEX,{"disambiguationData":[OD(0.0)],"derivedFrom":[subQ0,sQuery(id+"F0.wireOp",EDGE,"E20.9.0")]});Q98=makeQuery(id+"F1.opExtrude","CAP_EDGE",EDGE,{"disambiguationData":[OSD([subQ0]),TDD([makeQuery(id+"F0.imprint","IMPRINT",EDGE,{"disambiguationData":[TD([[subQ1,1.0]])],"derivedFrom":subQ0}),makeQuery(id+"F0.imprint","IMPRINT",EDGE,{"disambiguationData":[TD([[subQ1,-1.0]])],"derivedFrom":subQ0})])],"isStart":false});}
            var Q99;
            {var subQ0=sQuery(id+"F0.wireOp",EDGE,"E9");var subQ1=makeQuery(id+"F0.imprint","INTERSECT",VERTEX,{"disambiguationData":[OD(0.0)],"derivedFrom":[subQ0,sQuery(id+"F0.wireOp",EDGE,"E19")]});Q99=makeQuery(id+"F1.opExtrude","CAP_EDGE",EDGE,{"disambiguationData":[OSD([subQ0]),TDD([makeQuery(id+"F0.imprint","IMPRINT",EDGE,{"disambiguationData":[TD([[makeQuery(id+"F0.imprint","INTERSECT",VERTEX,{"disambiguationData":[OD(1.0)],"derivedFrom":[subQ0,sQuery(id+"F0.wireOp",EDGE,"E20.1.0")]}),-1.0]])],"derivedFrom":subQ0}),makeQuery(id+"F0.imprint","IMPRINT",EDGE,{"disambiguationData":[TD([[subQ1,-1.0]])],"derivedFrom":subQ0})])],"isStart":false});}
            var Q100;
            {var subQ0=sQuery(id+"F0.wireOp",EDGE,"E8");var subQ1=makeQuery(id+"F0.imprint","INTERSECT",VERTEX,{"disambiguationData":[OD(0.0)],"derivedFrom":[subQ0,sQuery(id+"F0.wireOp",EDGE,"E24.9.0")]});Q100=makeQuery(id+"F1.opExtrude","CAP_EDGE",EDGE,{"disambiguationData":[OSD([subQ0]),TDD([makeQuery(id+"F0.imprint","IMPRINT",EDGE,{"disambiguationData":[TD([[subQ1,1.0]])],"derivedFrom":subQ0}),makeQuery(id+"F0.imprint","IMPRINT",EDGE,{"disambiguationData":[TD([[subQ1,-1.0]])],"derivedFrom":subQ0})])],"isStart":false});}
            var Q101;
            {var subQ0=sQuery(id+"F0.wireOp",EDGE,"E8");var subQ1=makeQuery(id+"F0.imprint","INTERSECT",VERTEX,{"disambiguationData":[OD(0.0)],"derivedFrom":[subQ0,sQuery(id+"F0.wireOp",EDGE,"E22")]});Q101=makeQuery(id+"F1.opExtrude","CAP_EDGE",EDGE,{"disambiguationData":[OSD([subQ0]),TDD([makeQuery(id+"F0.imprint","IMPRINT",EDGE,{"disambiguationData":[TD([[makeQuery(id+"F0.imprint","INTERSECT",VERTEX,{"disambiguationData":[OD(1.0)],"derivedFrom":[subQ0,sQuery(id+"F0.wireOp",EDGE,"E24.1.0")]}),-1.0]])],"derivedFrom":subQ0}),makeQuery(id+"F0.imprint","IMPRINT",EDGE,{"disambiguationData":[TD([[subQ1,-1.0]])],"derivedFrom":subQ0})])],"isStart":false});}
            var Q102;
            {var subQ0=sQuery(id+"F0.wireOp",EDGE,"E7");var subQ1=makeQuery(id+"F0.imprint","INTERSECT",VERTEX,{"disambiguationData":[OD(0.0)],"derivedFrom":[subQ0,sQuery(id+"F0.wireOp",EDGE,"E23.9.0")]});Q102=makeQuery(id+"F1.opExtrude","CAP_EDGE",EDGE,{"disambiguationData":[OSD([subQ0]),TDD([makeQuery(id+"F0.imprint","IMPRINT",EDGE,{"disambiguationData":[TD([[subQ1,1.0]])],"derivedFrom":subQ0}),makeQuery(id+"F0.imprint","IMPRINT",EDGE,{"disambiguationData":[TD([[subQ1,-1.0]])],"derivedFrom":subQ0})])],"isStart":false});}
            var Q103;
            {var subQ0=sQuery(id+"F0.wireOp",EDGE,"E20.4.0");var subQ1=sQuery(id+"F0.wireOp",EDGE,"E9");Q103=makeQuery(id+"F1.opExtrude","SWEPT_EDGE",EDGE,{"disambiguationData":[OSD([subQ1,subQ0]),TDD([makeQuery(id+"F0.imprint","INTERSECT",VERTEX,{"disambiguationData":[OD(1.0)],"derivedFrom":[subQ1,subQ0]})])]});}
            var Q104;
            {var subQ0=sQuery(id+"F0.wireOp",EDGE,"E7");var subQ1=makeQuery(id+"F0.imprint","INTERSECT",VERTEX,{"disambiguationData":[OD(0.0)],"derivedFrom":[subQ0,sQuery(id+"F0.wireOp",EDGE,"E21")]});Q104=makeQuery(id+"F1.opExtrude","CAP_EDGE",EDGE,{"disambiguationData":[OSD([subQ0]),TDD([makeQuery(id+"F0.imprint","IMPRINT",EDGE,{"disambiguationData":[TD([[makeQuery(id+"F0.imprint","INTERSECT",VERTEX,{"disambiguationData":[OD(1.0)],"derivedFrom":[subQ0,sQuery(id+"F0.wireOp",EDGE,"E23.1.0")]}),-1.0]])],"derivedFrom":subQ0}),makeQuery(id+"F0.imprint","IMPRINT",EDGE,{"disambiguationData":[TD([[subQ1,-1.0]])],"derivedFrom":subQ0})])],"isStart":true});}
            var Q105;
            {var subQ0=sQuery(id+"F0.wireOp",EDGE,"E8");var subQ1=makeQuery(id+"F0.imprint","INTERSECT",VERTEX,{"disambiguationData":[OD(0.0)],"derivedFrom":[subQ0,sQuery(id+"F0.wireOp",EDGE,"E24.9.0")]});Q105=makeQuery(id+"F1.opExtrude","CAP_EDGE",EDGE,{"disambiguationData":[OSD([subQ0]),TDD([makeQuery(id+"F0.imprint","IMPRINT",EDGE,{"disambiguationData":[TD([[subQ1,1.0]])],"derivedFrom":subQ0}),makeQuery(id+"F0.imprint","IMPRINT",EDGE,{"disambiguationData":[TD([[subQ1,-1.0]])],"derivedFrom":subQ0})])],"isStart":true});}
            var Q106;
            {var subQ0=sQuery(id+"F0.wireOp",EDGE,"E8");var subQ1=makeQuery(id+"F0.imprint","INTERSECT",VERTEX,{"disambiguationData":[OD(0.0)],"derivedFrom":[subQ0,sQuery(id+"F0.wireOp",EDGE,"E22")]});Q106=makeQuery(id+"F1.opExtrude","CAP_EDGE",EDGE,{"disambiguationData":[OSD([subQ0]),TDD([makeQuery(id+"F0.imprint","IMPRINT",EDGE,{"disambiguationData":[TD([[makeQuery(id+"F0.imprint","INTERSECT",VERTEX,{"disambiguationData":[OD(1.0)],"derivedFrom":[subQ0,sQuery(id+"F0.wireOp",EDGE,"E24.1.0")]}),-1.0]])],"derivedFrom":subQ0}),makeQuery(id+"F0.imprint","IMPRINT",EDGE,{"disambiguationData":[TD([[subQ1,-1.0]])],"derivedFrom":subQ0})])],"isStart":true});}
            var Q107;
            {var subQ0=sQuery(id+"F0.wireOp",EDGE,"E9");var subQ1=makeQuery(id+"F0.imprint","INTERSECT",VERTEX,{"disambiguationData":[OD(0.0)],"derivedFrom":[subQ0,sQuery(id+"F0.wireOp",EDGE,"E20.9.0")]});Q107=makeQuery(id+"F1.opExtrude","CAP_EDGE",EDGE,{"disambiguationData":[OSD([subQ0]),TDD([makeQuery(id+"F0.imprint","IMPRINT",EDGE,{"disambiguationData":[TD([[subQ1,1.0]])],"derivedFrom":subQ0}),makeQuery(id+"F0.imprint","IMPRINT",EDGE,{"disambiguationData":[TD([[subQ1,-1.0]])],"derivedFrom":subQ0})])],"isStart":true});}
            var Q108;
            {var subQ0=sQuery(id+"F0.wireOp",EDGE,"E9");var subQ1=makeQuery(id+"F0.imprint","INTERSECT",VERTEX,{"disambiguationData":[OD(0.0)],"derivedFrom":[subQ0,sQuery(id+"F0.wireOp",EDGE,"E19")]});Q108=makeQuery(id+"F1.opExtrude","CAP_EDGE",EDGE,{"disambiguationData":[OSD([subQ0]),TDD([makeQuery(id+"F0.imprint","IMPRINT",EDGE,{"disambiguationData":[TD([[makeQuery(id+"F0.imprint","INTERSECT",VERTEX,{"disambiguationData":[OD(1.0)],"derivedFrom":[subQ0,sQuery(id+"F0.wireOp",EDGE,"E20.1.0")]}),-1.0]])],"derivedFrom":subQ0}),makeQuery(id+"F0.imprint","IMPRINT",EDGE,{"disambiguationData":[TD([[subQ1,-1.0]])],"derivedFrom":subQ0})])],"isStart":true});}
            var Q109;
            {var subQ0=sQuery(id+"F0.wireOp",EDGE,"E11");Q109=makeQuery(id+"F2.opShell","OFFSET_EDGE",EDGE,{"disambiguationData":[OSD([subQ0]),TDD([makeQuery(id+"F1.opExtrude","CAP_EDGE",EDGE,{"disambiguationData":[OSD([subQ0])],"isStart":true})])]});}
            var Q110;
            {var subQ0=sQuery(id+"F0.wireOp",EDGE,"E0");Q110=makeQuery(id+"F2.opShell","OFFSET_EDGE",EDGE,{"disambiguationData":[OSD([subQ0]),TDD([makeQuery(id+"F1.opExtrude","CAP_EDGE",EDGE,{"disambiguationData":[OSD([subQ0])],"isStart":true})]),OD(1.0)]});}
            var Q111;
            {var subQ0=sQuery(id+"F0.wireOp",EDGE,"E2");Q111=makeQuery(id+"F2.opShell","OFFSET_EDGE",EDGE,{"disambiguationData":[OSD([subQ0]),TDD([makeQuery(id+"F1.opExtrude","CAP_EDGE",EDGE,{"disambiguationData":[OSD([subQ0])],"isStart":true})]),OD(0.0)]});}
            var Q112;
            {var subQ0=sQuery(id+"F0.wireOp",EDGE,"E1");Q112=makeQuery(id+"F2.opShell","OFFSET_EDGE",EDGE,{"disambiguationData":[OSD([subQ0]),TDD([makeQuery(id+"F1.opExtrude","CAP_EDGE",EDGE,{"disambiguationData":[OSD([subQ0])],"isStart":true})]),OD(1.0)]});}
            var Q113;
            {var subQ0=sQuery(id+"F0.wireOp",EDGE,"E1");Q113=makeQuery(id+"F2.opShell","OFFSET_EDGE",EDGE,{"disambiguationData":[OSD([subQ0]),TDD([makeQuery(id+"F1.opExtrude","CAP_EDGE",EDGE,{"disambiguationData":[OSD([subQ0])],"isStart":true})]),OD(0.0)]});}
            var Q114;
            {var subQ0=sQuery(id+"F0.wireOp",EDGE,"E0");Q114=makeQuery(id+"F2.opShell","OFFSET_EDGE",EDGE,{"disambiguationData":[OSD([subQ0]),TDD([makeQuery(id+"F1.opExtrude","CAP_EDGE",EDGE,{"disambiguationData":[OSD([subQ0])],"isStart":true})]),OD(0.0)]});}
            var Q115;
            {var subQ0=sQuery(id+"F0.wireOp",EDGE,"E3");Q115=makeQuery(id+"F2.opShell","OFFSET_EDGE",EDGE,{"disambiguationData":[OSD([subQ0]),TDD([makeQuery(id+"F1.opExtrude","CAP_EDGE",EDGE,{"disambiguationData":[OSD([subQ0])],"isStart":true})]),OD(0.0)]});}
            var Q116;
            {var subQ0=sQuery(id+"F0.wireOp",EDGE,"E10");Q116=makeQuery(id+"F2.opShell","OFFSET_EDGE",EDGE,{"disambiguationData":[OSD([subQ0]),TDD([makeQuery(id+"F1.opExtrude","CAP_EDGE",EDGE,{"disambiguationData":[OSD([subQ0])],"isStart":true})])]});}
            var Q117;
            {var subQ0=sQuery(id+"F0.wireOp",EDGE,"E3");Q117=makeQuery(id+"F2.opShell","OFFSET_EDGE",EDGE,{"disambiguationData":[OSD([subQ0]),TDD([makeQuery(id+"F1.opExtrude","CAP_EDGE",EDGE,{"disambiguationData":[OSD([subQ0])],"isStart":true})]),OD(1.0)]});}
            var Q118;
            {var subQ0=sQuery(id+"F0.wireOp",EDGE,"E2");Q118=makeQuery(id+"F2.opShell","OFFSET_EDGE",EDGE,{"disambiguationData":[OSD([subQ0]),TDD([makeQuery(id+"F1.opExtrude","CAP_EDGE",EDGE,{"disambiguationData":[OSD([subQ0])],"isStart":true})]),OD(1.0)]});}
            var Q119;
            {var subQ0=sQuery(id+"F0.wireOp",EDGE,"E0");Q119=makeQuery(id+"F2.opShell","OFFSET_EDGE",EDGE,{"disambiguationData":[OSD([subQ0]),TDD([makeQuery(id+"F1.opExtrude","CAP_EDGE",EDGE,{"disambiguationData":[OSD([subQ0])],"isStart":true})]),OD(2.0)]});}
            var Q120;
            {var subQ0=sQuery(id+"F0.wireOp",EDGE,"E12");Q120=makeQuery(id+"F2.opShell","OFFSET_EDGE",EDGE,{"disambiguationData":[OSD([subQ0]),TDD([makeQuery(id+"F1.opExtrude","CAP_EDGE",EDGE,{"disambiguationData":[OSD([subQ0])],"isStart":true})])]});}
            var Q121;
            {var subQ0=sQuery(id+"F0.wireOp",EDGE,"E1");Q121=makeQuery(id+"F2.opShell","OFFSET_EDGE",EDGE,{"disambiguationData":[OSD([subQ0]),TDD([makeQuery(id+"F1.opExtrude","CAP_EDGE",EDGE,{"disambiguationData":[OSD([subQ0])],"isStart":false})]),OD(1.0)]});}
            var Q122;
            {var subQ0=sQuery(id+"F0.wireOp",EDGE,"E11");Q122=makeQuery(id+"F2.opShell","OFFSET_EDGE",EDGE,{"disambiguationData":[OSD([subQ0]),TDD([makeQuery(id+"F1.opExtrude","CAP_EDGE",EDGE,{"disambiguationData":[OSD([subQ0])],"isStart":false})])]});}
            var Q123;
            {var subQ0=sQuery(id+"F0.wireOp",EDGE,"E0");Q123=makeQuery(id+"F2.opShell","OFFSET_EDGE",EDGE,{"disambiguationData":[OSD([subQ0]),TDD([makeQuery(id+"F1.opExtrude","CAP_EDGE",EDGE,{"disambiguationData":[OSD([subQ0])],"isStart":false})]),OD(1.0)]});}
            var Q124;
            {var subQ0=sQuery(id+"F0.wireOp",EDGE,"E2");Q124=makeQuery(id+"F2.opShell","OFFSET_EDGE",EDGE,{"disambiguationData":[OSD([subQ0]),TDD([makeQuery(id+"F1.opExtrude","CAP_EDGE",EDGE,{"disambiguationData":[OSD([subQ0])],"isStart":false})]),OD(0.0)]});}
            var Q125;
            {var subQ0=sQuery(id+"F0.wireOp",EDGE,"E3");Q125=makeQuery(id+"F2.opShell","OFFSET_EDGE",EDGE,{"disambiguationData":[OSD([subQ0]),TDD([makeQuery(id+"F1.opExtrude","CAP_EDGE",EDGE,{"disambiguationData":[OSD([subQ0])],"isStart":false})]),OD(1.0)]});}
            var Q126;
            {var subQ0=sQuery(id+"F0.wireOp",EDGE,"E0");Q126=makeQuery(id+"F2.opShell","OFFSET_EDGE",EDGE,{"disambiguationData":[OSD([subQ0]),TDD([makeQuery(id+"F1.opExtrude","CAP_EDGE",EDGE,{"disambiguationData":[OSD([subQ0])],"isStart":false})]),OD(2.0)]});}
            var Q127;
            {var subQ0=sQuery(id+"F0.wireOp",EDGE,"E2");Q127=makeQuery(id+"F2.opShell","OFFSET_EDGE",EDGE,{"disambiguationData":[OSD([subQ0]),TDD([makeQuery(id+"F1.opExtrude","CAP_EDGE",EDGE,{"disambiguationData":[OSD([subQ0])],"isStart":false})]),OD(1.0)]});}
            var Q128;
            {var subQ0=sQuery(id+"F0.wireOp",EDGE,"E12");Q128=makeQuery(id+"F2.opShell","OFFSET_EDGE",EDGE,{"disambiguationData":[OSD([subQ0]),TDD([makeQuery(id+"F1.opExtrude","CAP_EDGE",EDGE,{"disambiguationData":[OSD([subQ0])],"isStart":false})])]});}
            var Q129;
            {var subQ0=sQuery(id+"F0.wireOp",EDGE,"E0");Q129=makeQuery(id+"F2.opShell","OFFSET_EDGE",EDGE,{"disambiguationData":[OSD([subQ0]),TDD([makeQuery(id+"F1.opExtrude","CAP_EDGE",EDGE,{"disambiguationData":[OSD([subQ0])],"isStart":false})]),OD(0.0)]});}
            var Q130;
            {var subQ0=sQuery(id+"F0.wireOp",EDGE,"E3");Q130=makeQuery(id+"F2.opShell","OFFSET_EDGE",EDGE,{"disambiguationData":[OSD([subQ0]),TDD([makeQuery(id+"F1.opExtrude","CAP_EDGE",EDGE,{"disambiguationData":[OSD([subQ0])],"isStart":false})]),OD(0.0)]});}
            var Q131;
            {var subQ0=sQuery(id+"F0.wireOp",EDGE,"E10");Q131=makeQuery(id+"F2.opShell","OFFSET_EDGE",EDGE,{"disambiguationData":[OSD([subQ0]),TDD([makeQuery(id+"F1.opExtrude","CAP_EDGE",EDGE,{"disambiguationData":[OSD([subQ0])],"isStart":false})])]});}
            var Q132;
            {var subQ0=sQuery(id+"F0.wireOp",EDGE,"E1");Q132=makeQuery(id+"F2.opShell","OFFSET_EDGE",EDGE,{"disambiguationData":[OSD([subQ0]),TDD([makeQuery(id+"F1.opExtrude","CAP_EDGE",EDGE,{"disambiguationData":[OSD([subQ0])],"isStart":false})]),OD(0.0)]});}
            var Q133;
            Q133=makeQuery(id+"F1.opExtrude","CAP_EDGE",EDGE,{"disambiguationData":[OSD([sQuery(id+"F0.wireOp",EDGE,"E20.7.0")])],"isStart":false});
            var Q134;
            Q134=makeQuery(id+"F1.opExtrude","CAP_EDGE",EDGE,{"disambiguationData":[OSD([sQuery(id+"F0.wireOp",EDGE,"E20.4.0")])],"isStart":false});
            var Q135;
            Q135=makeQuery(id+"F1.opExtrude","CAP_EDGE",EDGE,{"disambiguationData":[OSD([sQuery(id+"F0.wireOp",EDGE,"E20.3.0")])],"isStart":false});
            var Q136;
            Q136=makeQuery(id+"F1.opExtrude","CAP_EDGE",EDGE,{"disambiguationData":[OSD([sQuery(id+"F0.wireOp",EDGE,"E20.2.0")])],"isStart":false});
            var Q137;
            Q137=makeQuery(id+"F1.opExtrude","CAP_EDGE",EDGE,{"disambiguationData":[OSD([sQuery(id+"F0.wireOp",EDGE,"E20.1.0")])],"isStart":false});
            var Q138;
            Q138=makeQuery(id+"F1.opExtrude","CAP_EDGE",EDGE,{"disambiguationData":[OSD([sQuery(id+"F0.wireOp",EDGE,"E20.5.0")])],"isStart":false});
            var Q139;
            Q139=makeQuery(id+"F1.opExtrude","CAP_EDGE",EDGE,{"disambiguationData":[OSD([sQuery(id+"F0.wireOp",EDGE,"E20.6.0")])],"isStart":false});
            var Q140;
            Q140=makeQuery(id+"F1.opExtrude","CAP_EDGE",EDGE,{"disambiguationData":[OSD([sQuery(id+"F0.wireOp",EDGE,"E11")])],"isStart":false});
            fillet(context, id + "F3", {"entities" : qUnion([Q0, Q1, Q2, Q3, Q4, Q5, Q6, Q7, Q8, Q9, Q10, Q11, Q12, Q13, Q14, Q15, Q16, Q17, Q18, Q19, Q20, Q21, Q22, Q23, Q24, Q25, Q26, Q27, Q28, Q29, Q30, Q31, Q32, Q33, Q34, Q35, Q36, Q37, Q38, Q39, Q40, Q41, Q42, Q43, Q44, Q45, Q46, Q47, Q48, Q49, Q50, Q51, Q52, Q53, Q54, Q55, Q56, Q57, Q58, Q59, Q60, Q61, Q62, Q63, Q64, Q65, Q66, Q67, Q68, Q69, Q70, Q71, Q72, Q73, Q74, Q75, Q76, Q77, Q78, Q79, Q80, Q81, Q82, Q83, Q84, Q85, Q86, Q87, Q88, Q89, Q90, Q91, Q92, Q93, Q94, Q95, Q96, Q97, Q98, Q99, Q100, Q101, Q102, Q103, Q104, Q105, Q106, Q107, Q108, Q109, Q110, Q111, Q112, Q113, Q114, Q115, Q116, Q117, Q118, Q119, Q120, Q121, Q122, Q123, Q124, Q125, Q126, Q127, Q128, Q129, Q130, Q131, Q132, Q133, Q134, Q135, Q136, Q137, Q138, Q139, Q140]), "radius" : 0.64 * mm, "tangentPropagation" : true, "allowEdgeOverflow" : false});
        }
    });
